FCSTD DOCUMENT  (FreeCAD 0.19R24276 (Git))
Label: Balka_3
License: All rights reserved
LicenseURL: http://en.wikipedia.org/wiki/All_rights_reserved
objects: Sketcher::SketchObject×2, PartDesign::Body×1
note: 3 computed .brp shape members not serialized (recipe doc carries the construction recipe); baked Part::Feature solids carry a one-line shape summary decoded from their .brp

FEATURE [Sketcher::SketchObject] Sketch
  FullyConstrained = false
  MapMode = 5
  Support = -> [XY_Plane]
  sketch-geometry (6):
    g0: Circle CenterX=0 CenterY=0 CenterZ=0 NormalX=0 NormalY=0 NormalZ=1 AngleXU=0 Radius=2.5
    g1: ArcOfCircle CenterX=0 CenterY=0 CenterZ=0 NormalX=0 NormalY=0 NormalZ=1 AngleXU=0 Radius=3.5 StartAngle=1.5708 EndAngle=4.71239
    g2: Circle CenterX=58 CenterY=0 CenterZ=0 NormalX=0 NormalY=0 NormalZ=1 AngleXU=0 Radius=2.5
    g3: ArcOfCircle CenterX=58 CenterY=0 CenterZ=0 NormalX=0 NormalY=0 NormalZ=1 AngleXU=0 Radius=3.5 StartAngle=4.71052 EndAngle=7.85398
    g4: LineSegment StartX=-2.83801e-06 StartY=3.5 StartZ=0 EndX=58 EndY=3.5 EndZ=0
    g5: LineSegment StartX=58 StartY=-3.5 StartZ=0 EndX=0 EndY=-3.5 EndZ=0
  constraints (17):
    c: Coincident(g0,g-1)
    c: Coincident(g1,g0)
    c: PointOnObject(g2,g-1)
    c: Coincident(g3,g2)
    c: Equal(g1,g3)
    c: Equal(g0,g2)
    c: Diameter(g1) = 7
    c: DistanceX(g0,g2) = 58
    c: Horizontal(g4)
    c: Horizontal(g5)
    c: DistanceX(g5,g0) = 0
    c: DistanceX(g2,g5) = 0
    c: DistanceY(g5,g4) = 7
    c: PointOnObject(g3,g4)
    c: Coincident(g1,g4)
    c: PointOnObject(g1,g5)
    c: Diameter(g2) = 5
FEATURE [Sketcher::SketchObject] Sketch001
  FullyConstrained = false
  MapMode = 5
  Placement = pos=(0,0,5) rot=(0,0,1;0rad)
  sketch-geometry (13):
    g0: LineSegment StartX=0 StartY=0 StartZ=0 EndX=58 EndY=0 EndZ=0
    g1: LineSegment StartX=29 StartY=0 StartZ=0 EndX=29 EndY=16 EndZ=0
    g2: LineSegment StartX=28.5 StartY=16 StartZ=0 EndX=29.5 EndY=16 EndZ=0
    g3: Circle CenterX=0 CenterY=0 CenterZ=0 NormalX=0 NormalY=0 NormalZ=1 AngleXU=0 Radius=14
    g4: Circle CenterX=58 CenterY=0 CenterZ=0 NormalX=0 NormalY=0 NormalZ=1 AngleXU=0 Radius=14
    g5: LineSegment StartX=38.3086 StartY=-3.5 StartZ=0 EndX=19.6914 EndY=-3.5 EndZ=0
    g6: LineSegment StartX=28.5 StartY=6 StartZ=0 EndX=29.5 EndY=6 EndZ=0
    g7: LineSegment StartX=29.5 StartY=16 StartZ=0 EndX=29.5 EndY=6 EndZ=0
    g8: LineSegment StartX=28.5 StartY=16 StartZ=0 EndX=28.5 EndY=6 EndZ=0
    g9: ArcOfCircle CenterX=1.1e-15 CenterY=1e-15 CenterZ=0 NormalX=0 NormalY=0 NormalZ=1 AngleXU=0 Radius=20 StartAngle=6.10728 EndAngle=7.00194
    g10: ArcOfCircle CenterX=58 CenterY=0 CenterZ=0 NormalX=0 NormalY=0 NormalZ=1 AngleXU=0 Radius=20 StartAngle=2.42284 EndAngle=3.3175
    g11: LineSegment StartX=28.5 StartY=16 StartZ=0 EndX=15.0525 EndY=13.169 EndZ=0
    g12: LineSegment StartX=29.5 StartY=16 StartZ=0 EndX=42.9475 EndY=13.169 EndZ=0
  constraints (28):
    c: Coincident(g0,g-1)
    c: PointOnObject(g0,g-1)
    c: DistanceX(g0,g0) = 58
    c: Vertical(g1)
    c: Symmetric(g-1,g0,g1)
    c: DistanceY(g1,g1) = 16
    c: Horizontal(g2)
    c: Symmetric(g2,g2,g1)
    c: DistanceX(g2,g2) = 1
    c: Coincident(g3,g-1)
    c: Coincident(g4,g0)
    c: Diameter(g4) = 28
    c: Equal(g4,g3)
    c: Horizontal(g5)
    c: Horizontal(g6)
    c: Vertical(g7)
    c: Vertical(g8)
    c: Coincident(g8,g6)
    c: Coincident(g7,g6)
    c: DistanceY(g6,g2) = 10
    c: Diameter(g9) = 40
    c: Diameter(g10) = 40
    c: Coincident(g5,g10)
    c: Coincident(g5,g9)
    c: Coincident(g11,g8)
    c: Coincident(g11,g9)
    c: Coincident(g12,g7)
    c: Coincident(g12,g10)
FEATURE [PartDesign::Body] Body
  Group = -> [Sketch,Sketch001]
  Origin = -> Origin
